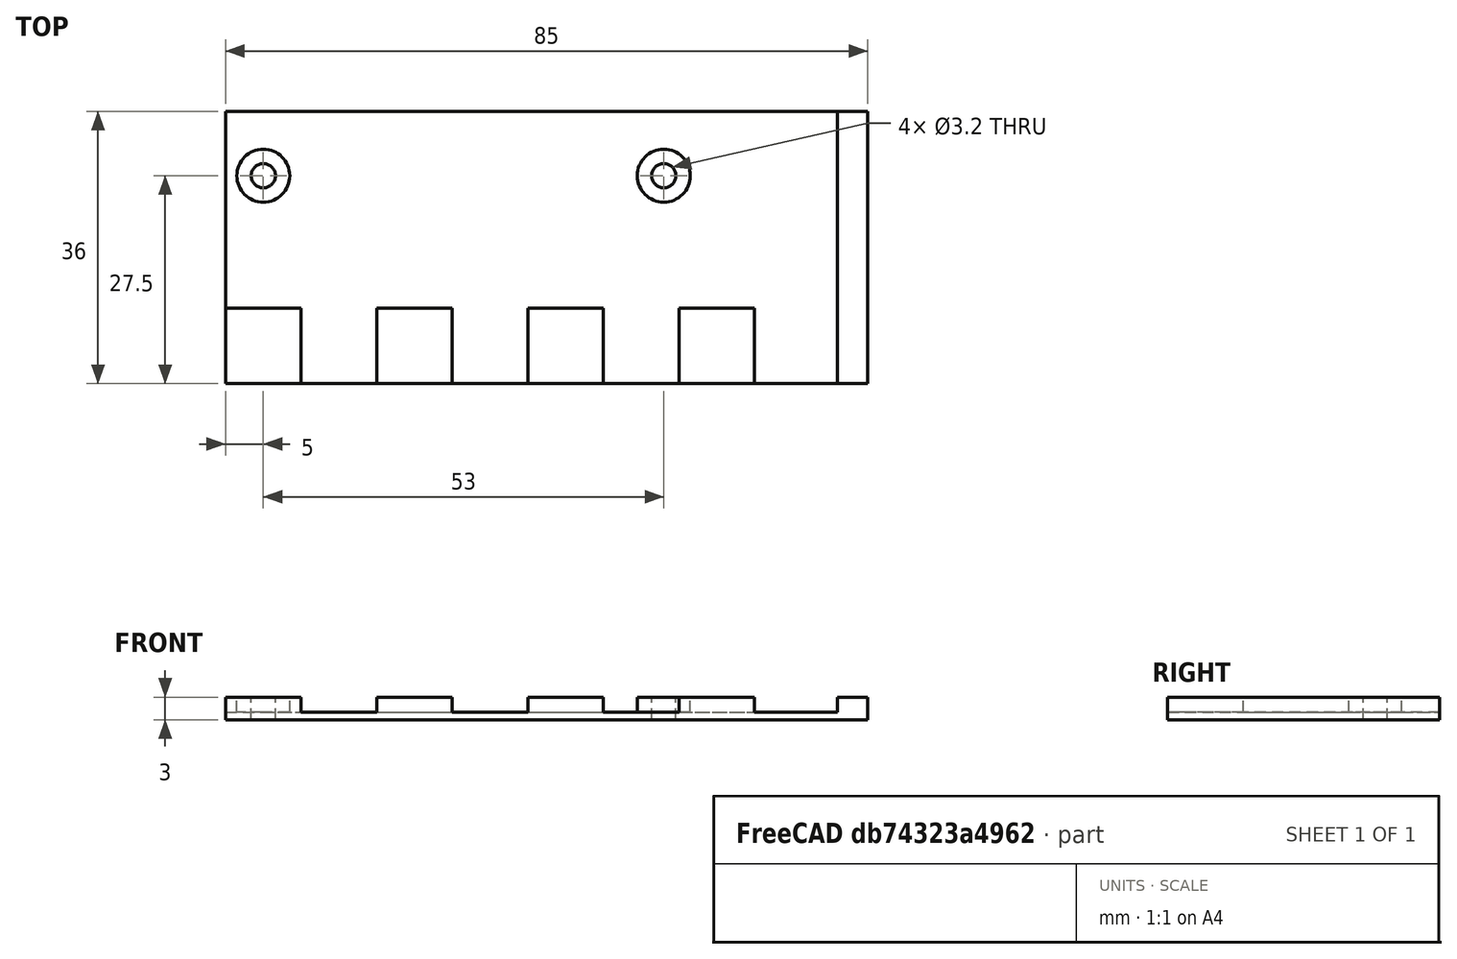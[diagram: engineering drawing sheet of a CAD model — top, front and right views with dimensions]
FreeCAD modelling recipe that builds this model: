
FCSTD DOCUMENT  (FreeCAD 0.18R14555 (Git shallow))
Label: justce-plus-rev7-mount
License: All rights reserved
LicenseURL: http://en.wikipedia.org/wiki/All_rights_reserved
objects: Part::Box×8, Part::Cylinder×4, Part::MultiFuse×3, Part::Cut×1, Part::Feature×1
note: 17 computed .brp shape members not serialized (recipe doc carries the construction recipe); baked Part::Feature solids carry a one-line shape summary decoded from their .brp

FEATURE [Part::Box] Box  label="Cube"
  AttacherType = Attacher::AttachEngine3D
  Height = 1
  Length = 5
  Width = 36
FEATURE [Part::Box] Box001  label="Cube001"
  AttacherType = Attacher::AttachEngine3D
  Height = 1
  Length = 53
  Placement = pos=(5,0,0) rot=(0,0,1;0rad)
  Width = 36
FEATURE [Part::Box] Box002  label="Cube002"
  AttacherType = Attacher::AttachEngine3D
  Height = 1
  Length = 27
  Placement = pos=(58,0,0) rot=(0,0,1;0rad)
  Width = 36
FEATURE [Part::Cylinder] Cylinder
  Angle = 360
  AttacherType = Attacher::AttachEngine3D
  Height = 3
  Placement = pos=(5,27.5,0) rot=(0,0,1;0rad)
  Radius = 3.5
FEATURE [Part::Cylinder] Cylinder001
  Angle = 360
  AttacherType = Attacher::AttachEngine3D
  Height = 3
  Placement = pos=(58,27.5,0) rot=(0,0,1;0rad)
  Radius = 3.5
FEATURE [Part::Cylinder] Cylinder002
  Angle = 360
  AttacherType = Attacher::AttachEngine3D
  Height = 3
  Placement = pos=(58,27.5,0) rot=(0,0,1;0rad)
  Radius = 1.6
FEATURE [Part::Cylinder] Cylinder003
  Angle = 360
  AttacherType = Attacher::AttachEngine3D
  Height = 3
  Placement = pos=(5,27.5,0) rot=(0,0,1;0rad)
  Radius = 1.6
FEATURE [Part::Box] Box003  label="Cube003"
  AttacherType = Attacher::AttachEngine3D
  Height = 3
  Length = 10
  Width = 10
FEATURE [Part::Box] Box004  label="Cube004"
  AttacherType = Attacher::AttachEngine3D
  Height = 3
  Length = 10
  Placement = pos=(60,0,0) rot=(0,0,1;0rad)
  Width = 10
FEATURE [Part::Box] Box005  label="Cube005"
  AttacherType = Attacher::AttachEngine3D
  Height = 3
  Length = 10
  Placement = pos=(20,0,0) rot=(0,0,1;0rad)
  Width = 10
FEATURE [Part::Box] Box006  label="Cube006"
  AttacherType = Attacher::AttachEngine3D
  Height = 3
  Length = 10
  Placement = pos=(40,0,0) rot=(0,0,1;0rad)
  Width = 10
FEATURE [Part::MultiFuse] Fusion
  Shapes = -> [Cylinder,Cylinder001,Box003,Box004,Box005,Box006,Box002,Box001,Box]
FEATURE [Part::MultiFuse] Fusion001
  Shapes = -> [Cylinder003,Cylinder002]
FEATURE [Part::Cut] Cut
  Base = -> Fusion
  Tool = -> Fusion001
FEATURE [Part::Box] Box007  label="Cube007"
  AttacherType = Attacher::AttachEngine3D
  Height = 3
  Length = 4
  Placement = pos=(81,0,0) rot=(0,0,1;0rad)
  Width = 36
FEATURE [Part::MultiFuse] Fusion002
  Shapes = -> [Box007,Cut]
FEATURE [Part::Feature] Fusion002001  label="Fusion003"
  shape: bbox 85 x 36 x 3 mm, 29 faces (baked)
